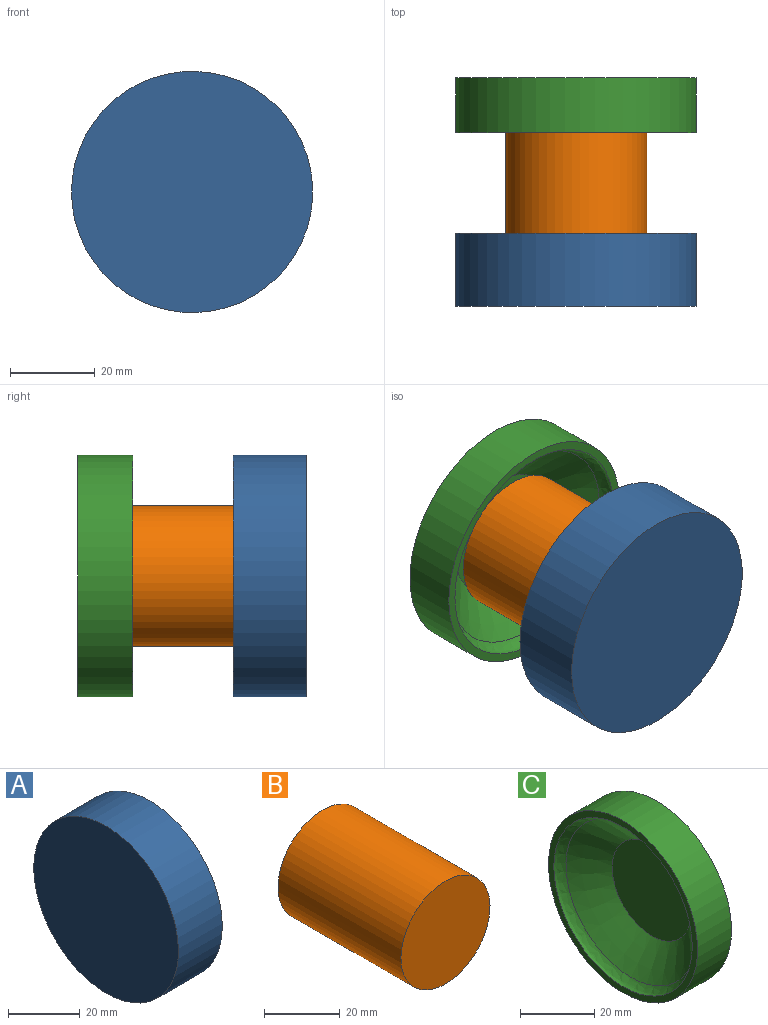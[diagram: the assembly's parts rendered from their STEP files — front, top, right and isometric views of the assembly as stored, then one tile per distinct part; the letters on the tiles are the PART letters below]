
ASSEMBLY  parts=3 mates=4
PART A: 10 faces, bbox 17.3x57x57 mm
  f0: torus R=18.97mm, axis (1,0,0), area 202.1mm2, adj f1,f9
  f1: cone r=20.43mm half-angle=43.3deg, axis (1,0,0), area 1139.6mm2, adj f0,f2
  f2: revolved ~52.99x52.99mm, area 341.3mm2, adj f1,f3
  f3: plane 56.99x56.99mm, normal (1,0,0), area 345.5mm2, adj f2,f4
  f4: cylinder r=28.5mm len=56.99mm, axis (1,0,0), area 3089.3mm2, adj f3,f5
  f5: plane 56.99x56.99mm, normal (-1,0,0), area 2550.9mm2, adj f4
  f6: plane 34x34mm, normal (1,0,0), area 907.9mm2, adj f7
  f7: cylinder r=17mm len=34mm, axis (1,0,0), area 640.9mm2, adj f6,f8
  f8: torus R=18mm, axis (1,0,0), area 171.4mm2, adj f7,f9
  f9: plane 37.95x37.95mm, normal (1,0,0), area 113.2mm2, adj f0,f8
PART B: 3 faces, bbox 33.3x46x33.3 mm
  f0: cylinder r=16.67mm len=46mm, axis (0,1,0), area 4818.1mm2, adj f1,f2
  f1: plane 33.34x33.34mm, normal (0,-1,0), area 873mm2, adj f0
  f2: plane 33.34x33.34mm, normal (0,1,0), area 873mm2, adj f0
PART C: 6 faces, bbox 13x57x57 mm
  f0: cylinder r=28.5mm len=56.99mm, axis (1,0,0), area 2322.5mm2, adj f1,f5
  f1: plane 56.99x56.99mm, normal (-1,0,0), area 351.9mm2, adj f0,f2
  f2: revolved ~52.91x52.91mm, area 570.4mm2, adj f1,f3
  f3: cone r=24.79mm half-angle=50.5deg, axis (-1,0,0), area 1574.1mm2, adj f2,f4
  f4: plane 30.2x30.2mm, normal (-1,0,0), area 716.3mm2, adj f3
  f5: plane 56.99x56.99mm, normal (1,0,0), area 2550.9mm2, adj f0
PLACE A rot(axis=(0.58,0.58,0.58),120deg) t=(-2.84,-17.62,-9.42)mm
PLACE B t=(-2.84,28.38,-9.42)mm
PLACE C rot(axis=(0.58,0.58,0.58),120deg) t=(-2.84,32.38,-9.42)mm
MATE planar B.f0 <-> C.f0  axis (0,1,0) through (-2.84,28.38,-9.42)mm
MATE cylindrical A.f0 <-> B.f0  axis (0,1,0) through (-2.84,-14.62,-9.42)mm
MATE planar A.f0 <-> B.f0  axis (0,1,0) through (-2.84,-17.62,-9.42)mm
MATE cylindrical C.f0 <-> B.f0  axis (0,-1,0) through (-2.84,28.38,-9.42)mm
